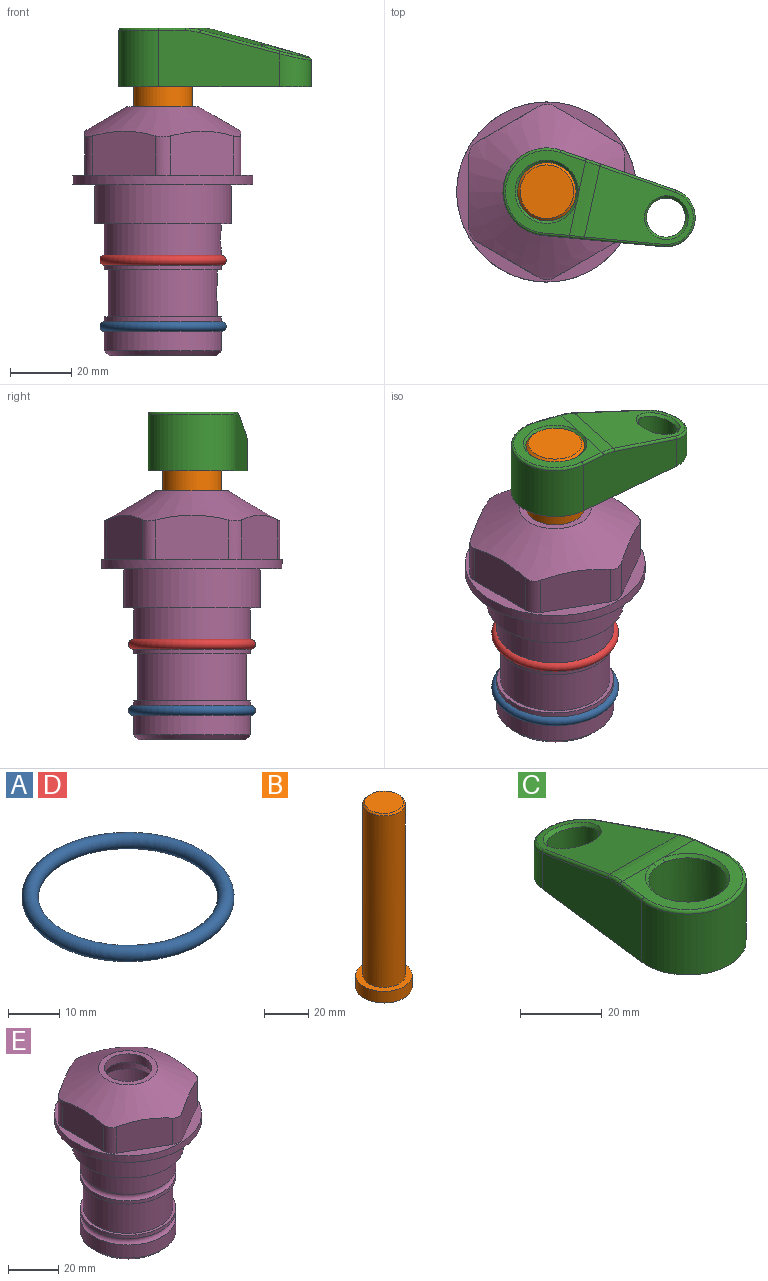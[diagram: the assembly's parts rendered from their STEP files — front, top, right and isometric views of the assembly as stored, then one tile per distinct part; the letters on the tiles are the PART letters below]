
ASSEMBLY  parts=5 mates=4
PART A: 1 faces, bbox 44.7x44.7x3.2 mm
  f0: torus R=19.05mm, axis (0,0,1), area 1193.9mm2
PART B: 6 faces, bbox 25.4x25.4x101.6 mm
  f0: plane 17.46x17.46mm, normal (0,0,1), area 239.5mm2, adj f5
  f1: plane 25.4x25.4mm, normal (0,0,-1), area 506.7mm2, adj f2
  f2: cylinder r=12.7mm len=25.4mm, axis (0,0,1), area 506.7mm2, adj f1,f3
  f3: plane 25.4x25.4mm, normal (0,0,1), area 221.7mm2, adj f2,f4
  f4: cylinder r=9.53mm len=94.46mm, axis (0,0,1), area 5653mm2, adj f3,f5
  f5: cone r=8.73mm half-angle=45deg, axis (0,0,-1), area 64.4mm2, adj f0,f4
PART C: 31 faces, bbox 31.7x65.5x19.8 mm
  f0: plane 39.12x18.26mm, normal (0.99,0.12,0), area 612.2mm2, adj f1,f4,f7,f11,f13,f15
  f1: cylinder r=9.53mm len=18.91mm, axis (0,0,-1), area 296.1mm2, adj f0,f2,f7,f17
  f2: plane 39.12x18.26mm, normal (-0.99,0.12,0), area 612.2mm2, adj f1,f4,f7,f12,f14,f16
  f3: cylinder r=6.35mm len=12.7mm, axis (0,0,-1), area 362.4mm2, adj f7,f18
  f4: cylinder r=14.29mm len=28.58mm, axis (0,0,-1), area 882.2mm2, adj f0,f2,f7,f10
  f5: cylinder r=9.53mm len=19.05mm, axis (0,0,-1), area 1092.6mm2, adj f7,f19,f20
  f6: plane 26.99x23.69mm, normal (0,0,1), area 216.2mm2, adj f9,f10,f11,f12,f19
  f7: plane 63.5x28.58mm, normal (0,0,-1), area 661.8mm2, adj f0,f1,f2,f3,f4,f5,f22,f23
  f8: plane 33.52x23.6mm, normal (0,0.26,0.97), area 486mm2, adj f9,f15,f16,f17,f18
  f9: cylinder r=19.05mm len=24.72mm, axis (1,0,0), area 120.4mm2, adj f6,f8,f13,f14,f20
  f10: torus R=13.49mm, axis (0,0,1), area 59mm2, adj f4,f6,f11,f12
  f11: cylinder r=0.79mm len=8.67mm, axis (0.12,-0.99,0), area 10.8mm2, adj f0,f6,f10,f13
  f12: cylinder r=0.79mm len=8.67mm, axis (0.12,0.99,0), area 10.8mm2, adj f2,f6,f10,f14
  f13: bspline ~4.95x1.42mm, area 6.1mm2, adj f0,f9,f11,f15
  f14: bspline ~4.95x1.42mm, area 6.1mm2, adj f2,f9,f12,f16
  f15: cylinder r=0.79mm len=25.95mm, axis (0.12,-0.96,0.26), area 32.9mm2, adj f0,f8,f13,f17
  f16: cylinder r=0.79mm len=25.95mm, axis (0.12,0.96,-0.26), area 32.9mm2, adj f2,f8,f14,f17
  f17: bspline ~18.91x8.38mm, area 30mm2, adj f1,f8,f15,f16
  f18: bspline ~14.29x14.29mm, area 48.3mm2, adj f3,f8
  f19: cone r=9.53mm half-angle=45deg, axis (0,0,1), area 66.5mm2, adj f5,f6,f20
  f20: bspline ~3.22x0.96mm, area 3.5mm2, adj f5,f9,f19
  f21: plane 2.75x2.72mm, normal (0,0,-1), area 2.9mm2, adj f23,f25,f28
  f22: plane 23.05x15.88mm, normal (-0.99,-0.12,0), area 323.6mm2, adj f7,f25,f26,f27,f28,f29
  f23: plane 23.05x15.88mm, normal (0.99,-0.12,0), area 323.6mm2, adj f7,f21,f25,f27,f28,f30
  f24: cylinder r=9.53mm len=10.69mm, axis (0,0,-1), area 114.7mm2, adj f7,f27,f29,f30
  f25: cylinder r=12.7mm len=20.59mm, axis (0,0,-1), area 381.1mm2, adj f7,f21,f22,f23,f26,f28
  f26: plane 2.75x2.72mm, normal (0,0,-1), area 2.9mm2, adj f22,f25,f28
  f27: plane 19.72x18.37mm, normal (0,-0.26,-0.97), area 291.8mm2, adj f22,f23,f24,f28,f29,f30
  f28: cylinder r=15.88mm len=19.92mm, axis (1,0,0), area 54.8mm2, adj f21,f22,f23,f25,f26,f27
  f29: cylinder r=1.59mm len=11mm, axis (0,0,-1), area 34.7mm2, adj f7,f22,f24,f27
  f30: cylinder r=1.59mm len=11mm, axis (0,0,-1), area 34.7mm2, adj f7,f23,f24,f27
PART D: same geometry as A
PART E: 36 faces, bbox 58.7x58.7x81 mm
  f0: cylinder r=17.78mm len=35.56mm, axis (0,0,1), area 1666.6mm2, adj f23,f24,f31
  f1: cylinder r=19.05mm len=38.1mm, axis (0,0,1), area 1187.7mm2, adj f26,f27,f30
  f2: plane 58.66x58.66mm, normal (0,0,-1), area 1150.6mm2, adj f3,f28
  f3: cylinder r=29.33mm len=58.66mm, axis (0,0,-1), area 585.1mm2, adj f2,f4
  f4: plane 58.66x58.66mm, normal (0,0,1), area 475.9mm2, adj f3,f5,f6,f7,f8,f9,f10,f11
  f5: plane 20.32x14.34mm, normal (-0.5,0.87,0), area 324.4mm2, adj f4,f15,f16,f17
  f6: plane 20.32x14.34mm, normal (0.5,0.87,0), area 324.4mm2, adj f4,f14,f15,f17
  f7: plane 23.48x14.34mm, normal (1,0,0), area 324.4mm2, adj f4,f13,f14,f17
  f8: plane 20.32x14.34mm, normal (0.5,-0.87,0), area 324.4mm2, adj f4,f12,f13,f17
  f9: plane 20.32x14.34mm, normal (-0.5,-0.87,0), area 324.4mm2, adj f4,f11,f12,f17
  f10: plane 23.48x14.34mm, normal (-1,0,0), area 324.4mm2, adj f4,f11,f16,f17
  f11: cylinder r=5.08mm len=12.85mm, axis (0,0,-1), area 67.2mm2, adj f4,f9,f10,f17
  f12: cylinder r=5.08mm len=12.85mm, axis (0,0,-1), area 67.2mm2, adj f4,f8,f9,f17
  f13: cylinder r=5.08mm len=12.85mm, axis (0,0,-1), area 67.2mm2, adj f4,f7,f8,f17
  f14: cylinder r=5.08mm len=12.85mm, axis (0,0,-1), area 67.2mm2, adj f4,f6,f7,f17
  f15: cylinder r=5.08mm len=12.85mm, axis (0,0,-1), area 67.2mm2, adj f4,f5,f6,f17
  f16: cylinder r=5.08mm len=12.85mm, axis (0,0,-1), area 67.2mm2, adj f4,f5,f10,f17
  f17: cone r=11.73mm half-angle=60deg, axis (0,0,-1), area 2071.8mm2, adj f5,f6,f7,f8,f9,f10,f11,f12
  f18: plane 23.46x23.46mm, normal (0,0,1), area 147.4mm2, adj f17,f35
  f19: plane 34.93x34.93mm, normal (0,0,-1), area 958mm2, adj f29
  f20: cylinder r=19.05mm len=38.1mm, axis (0,0,1), area 760.1mm2, adj f21,f29
  f21: torus R=19.05mm, axis (0,0,1), area 565.3mm2, adj f20,f22
  f22: cylinder r=19.05mm len=38.1mm, axis (0,0,1), area 190mm2, adj f21,f23
  f23: plane 38.1x38.1mm, normal (0,0,1), area 146.9mm2, adj f0,f22
  f24: plane 38.1x38.1mm, normal (0,0,-1), area 146.9mm2, adj f0,f25
  f25: cylinder r=19.05mm len=38.1mm, axis (0,0,1), area 190mm2, adj f24,f26
  f26: torus R=19.05mm, axis (0,0,1), area 565.3mm2, adj f1,f25
  f27: plane 44.45x44.45mm, normal (0,0,-1), area 411.7mm2, adj f1,f28
  f28: cylinder r=22.23mm len=44.45mm, axis (0,0,1), area 1773.5mm2, adj f2,f27
  f29: cone r=19.05mm half-angle=45deg, axis (0,0,1), area 257.5mm2, adj f19,f20
  f30: cylinder r=3.38mm len=6.81mm, axis (-1,0,0), area 136.4mm2, adj f1,f33
  f31: cylinder r=3.38mm len=6.76mm, axis (-1,0,0), area 109.2mm2, adj f0,f33
  f32: plane 25.4x25.4mm, normal (0,0,1), area 506.7mm2, adj f33
  f33: cylinder r=12.7mm len=66.42mm, axis (0,0,-1), area 5227.8mm2, adj f30,f31,f32,f34
  f34: cone r=9.53mm half-angle=30deg, axis (0,0,-1), area 443.4mm2, adj f33,f35
  f35: cylinder r=9.53mm len=19.05mm, axis (0,0,-1), area 240.9mm2, adj f18,f34
PLACE A t=(0,0,-21.59)mm
PLACE B rot(axis=(0,0,-1),102.2deg) t=(0,0,-12.45)mm
PLACE C rot(axis=(0,0,-1),102.2deg) t=(0,0,-12.45)mm
PLACE D at identity
PLACE E at identity fixed
MATE cylindrical B.f2 <-> E.f0  axis (0,0,1) through (0,0,-50.55)mm
MATE fastened E.f0 <-> D.f0  axis (0,0,1) through (0,0,-24.51)mm
MATE fastened B.f2 <-> C.f4  axis (0,0,1) through (0,0,51.05)mm
MATE fastened A.f0 <-> E.f0  axis (0,0,1) through (0,0,-46.1)mm
